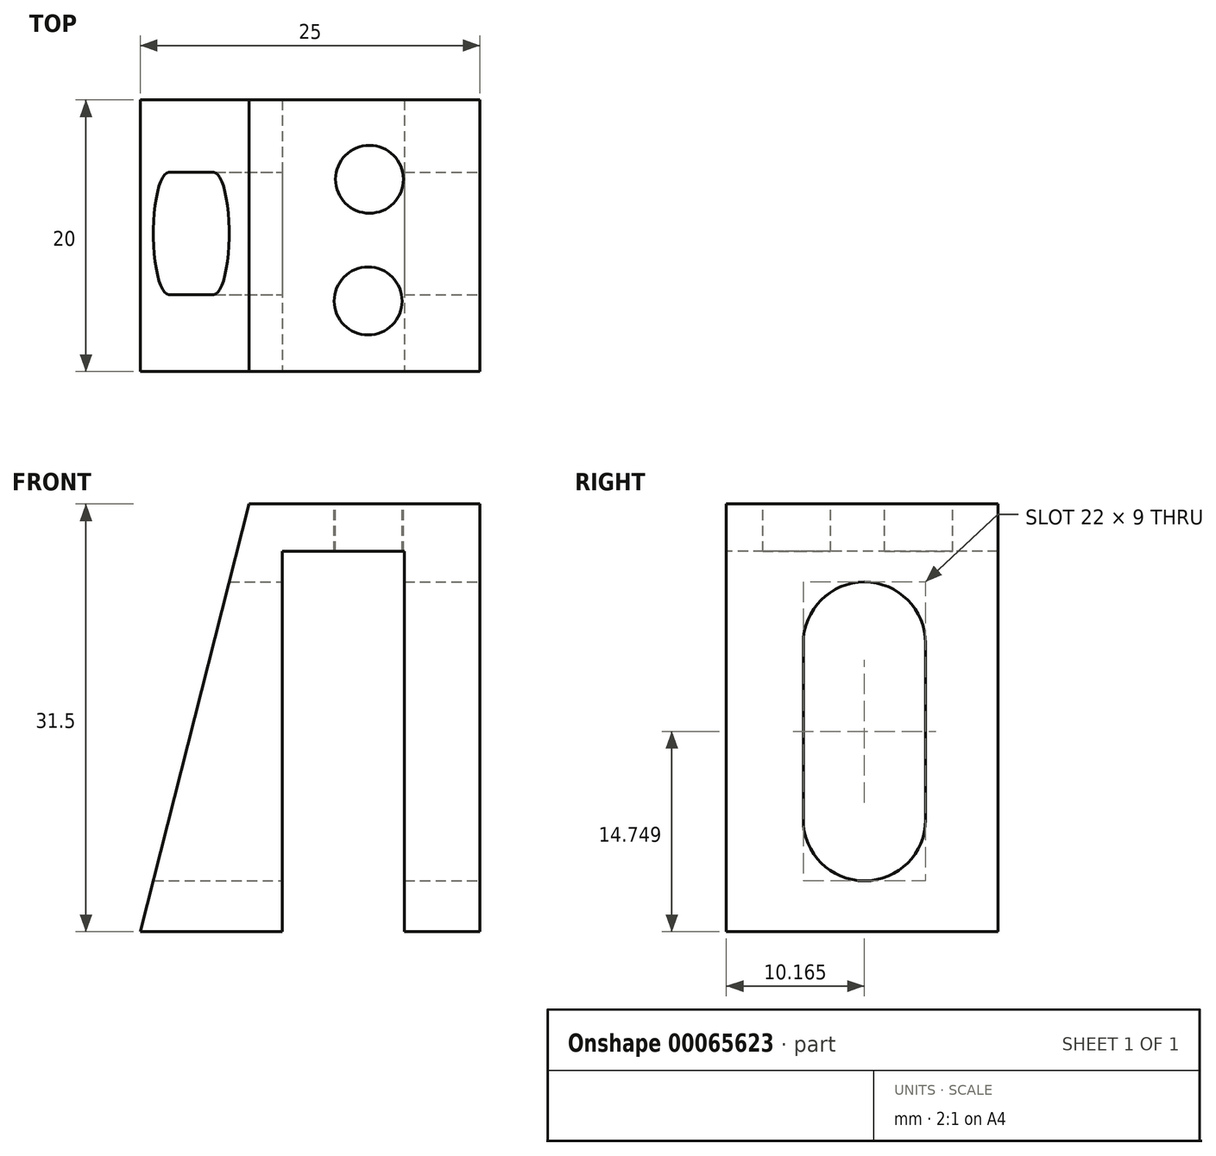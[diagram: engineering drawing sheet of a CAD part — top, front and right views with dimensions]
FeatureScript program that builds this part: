
annotation { "Feature Type Name" : "Feature", "Feature Type Description" : "" }
export const myFeature = defineFeature(function(context is Context, id is Id, definition is map)
    precondition{}
    {
        {
            var Q0;
            Q0=qCreatedBy(makeId("Front.planeOp"),FACE);
            var sketch = newSketch(context, id + "F0", { "sketchPlane" : qUnion([Q0])});
            skLineSegment(sketch, "E0", {"start": v(-57.09, 0) * mm, "end": v(-49.09, 31.5) * mm});
            skLineSegment(sketch, "E1", {"start": v(-49.09, 31.5) * mm, "end": v(-32.09, 31.5) * mm});
            skLineSegment(sketch, "E2", {"start": v(-32.09, 31.5) * mm, "end": v(-32.09, 0) * mm});
            skLineSegment(sketch, "E3", {"start": v(-32.09, 0) * mm, "end": v(-57.09, 0) * mm});
            skSolve(sketch);
        }
        {
            var Q0;
            Q0=makeQuery(id+"F0.imprint","IMPRINT",FACE,{"disambiguationData":[TD([[makeQuery(id+"F0.imprint","IMPRINT",EDGE,{"derivedFrom":sQuery(id+"F0.wireOp",EDGE,"E0")}),-1.0]])]});
            extrude(context, id + "F1", {"entities" : qUnion([Q0]), "depth" : 20 * mm});
        }
        {
            var Q0;
            Q0=makeQuery(id+"F1.opExtrude","SWEPT_FACE",FACE,{"disambiguationData":[OSD([sQuery(id+"F0.wireOp",EDGE,"E1")])]});
            var sketch = newSketch(context, id + "F2", { "sketchPlane" : qUnion([Q0])});
            skCircle(sketch, "E4", {"center": v(-40.23, -5.84) * mm, "radius": 2.5 * mm});
            skCircle(sketch, "E5", {"center": v(-40.33, -14.8) * mm, "radius": 2.5 * mm});
            skSolve(sketch);
        }
        {
            var Q0;
            Q0=makeQuery(id+"F2.imprint","IMPRINT",FACE,{"disambiguationData":[TD([[makeQuery(id+"F2.imprint","IMPRINT",EDGE,{"derivedFrom":sQuery(id+"F2.wireOp",EDGE,"E4")}),1.0]])]});
            var Q1;
            Q1=makeQuery(id+"F2.imprint","IMPRINT",FACE,{"disambiguationData":[TD([[makeQuery(id+"F2.imprint","IMPRINT",EDGE,{"derivedFrom":sQuery(id+"F2.wireOp",EDGE,"E5")}),1.0]])]});
            extrude(context, id + "F3", {"entities" : qUnion([Q0, Q1]), "operationType" : NewBodyOperationType.REMOVE, "oppositeDirection" : true, "depth" : 10 * mm});
        }
        {
            var Q0;
            Q0=makeQuery(id+"F1.opExtrude","CAP_FACE",FACE,{"disambiguationData":[OSD([sQuery(id+"F0.wireOp",EDGE,"E0"),sQuery(id+"F0.wireOp",EDGE,"E1"),sQuery(id+"F0.wireOp",EDGE,"E2"),sQuery(id+"F0.wireOp",EDGE,"E3")])],"isStart":false});
            var sketch = newSketch(context, id + "F4", { "sketchPlane" : qUnion([Q0])});
            skSolve(sketch);
        }
        {
            var Q0;
            Q0=makeQuery(id+"F4.imprint","IMPRINT",FACE,{"disambiguationData":[TD([[makeQuery(id+"F4.imprint","IMPRINT",EDGE,{"derivedFrom":makeQuery(id+"F1.opExtrude","CAP_EDGE",EDGE,{"disambiguationData":[OSD([sQuery(id+"F0.wireOp",EDGE,"E0")])],"isStart":false})}),-1.0]])]});
            var sketch = newSketch(context, id + "F5", { "sketchPlane" : qUnion([Q0])});
            skLineSegment(sketch, "E6.bottom", {"start": v(-37.65, 0) * mm, "end": v(-46.65, 0) * mm});
            skLineSegment(sketch, "E6.top", {"start": v(-37.65, 28) * mm, "end": v(-46.65, 28) * mm});
            skLineSegment(sketch, "E6.left", {"start": v(-37.65, 0) * mm, "end": v(-37.65, 28) * mm});
            skLineSegment(sketch, "E6.right", {"start": v(-46.65, 0) * mm, "end": v(-46.65, 28) * mm});
            skSolve(sketch);
        }
        {
            var Q0;
            Q0 = qSketchRegion(id + "F5", true);
            extrude(context, id + "F6", {"entities" : qUnion([Q0]), "operationType" : NewBodyOperationType.REMOVE, "oppositeDirection" : true, "depth" : 25 * mm});
        }
        {
            var Q0;
            Q0=makeQuery(id+"F1.opExtrude","SWEPT_FACE",FACE,{"disambiguationData":[OSD([sQuery(id+"F0.wireOp",EDGE,"E2")])]});
            var sketch = newSketch(context, id + "F7", { "sketchPlane" : qUnion([Q0])});
            skLineSegment(sketch, "E7.bottom", {"start": v(-14.33, 21.25) * mm, "end": v(-5.33, 21.25) * mm});
            skLineSegment(sketch, "E7.top", {"start": v(-14.33, 8.25) * mm, "end": v(-5.33, 8.25) * mm});
            skLineSegment(sketch, "E7.left", {"start": v(-14.33, 21.25) * mm, "end": v(-14.33, 8.25) * mm});
            skLineSegment(sketch, "E7.right", {"start": v(-5.33, 21.25) * mm, "end": v(-5.33, 8.25) * mm});
            skArc(sketch, "E8", {"start": v(-5.33, 21.25) * mm, "mid": v(-9.83, 25.75) * mm, "end": v(-14.33, 21.25) * mm});
            skArc(sketch, "E9", {"start": v(-14.33, 8.25) * mm, "mid": v(-9.83, 3.75) * mm, "end": v(-5.33, 8.25) * mm});
            skSolve(sketch);
        }
        {
            var Q0;
            Q0 = qSketchRegion(id + "F7", true);
            var Q1;
            Q1=makeQuery(id+"F7.imprint","IMPRINT",FACE,{"disambiguationData":[TD([[makeQuery(id+"F7.imprint","IMPRINT",EDGE,{"derivedFrom":sQuery(id+"F7.wireOp",EDGE,"E7.bottom")}),1.0]])]});
            var Q2;
            Q2=makeQuery(id+"F7.imprint","IMPRINT",FACE,{"disambiguationData":[TD([[makeQuery(id+"F7.imprint","IMPRINT",EDGE,{"derivedFrom":sQuery(id+"F7.wireOp",EDGE,"E7.bottom")}),-1.0]])]});
            var Q3;
            Q3=makeQuery(id+"F7.imprint","IMPRINT",FACE,{"disambiguationData":[TD([[makeQuery(id+"F7.imprint","IMPRINT",EDGE,{"derivedFrom":sQuery(id+"F7.wireOp",EDGE,"E7.top")}),-1.0]])]});
            extrude(context, id + "F8", {"entities" : qUnion([Q0, Q1, Q2, Q3]), "operationType" : NewBodyOperationType.REMOVE, "oppositeDirection" : true, "depth" : 25 * mm});
        }
    });
